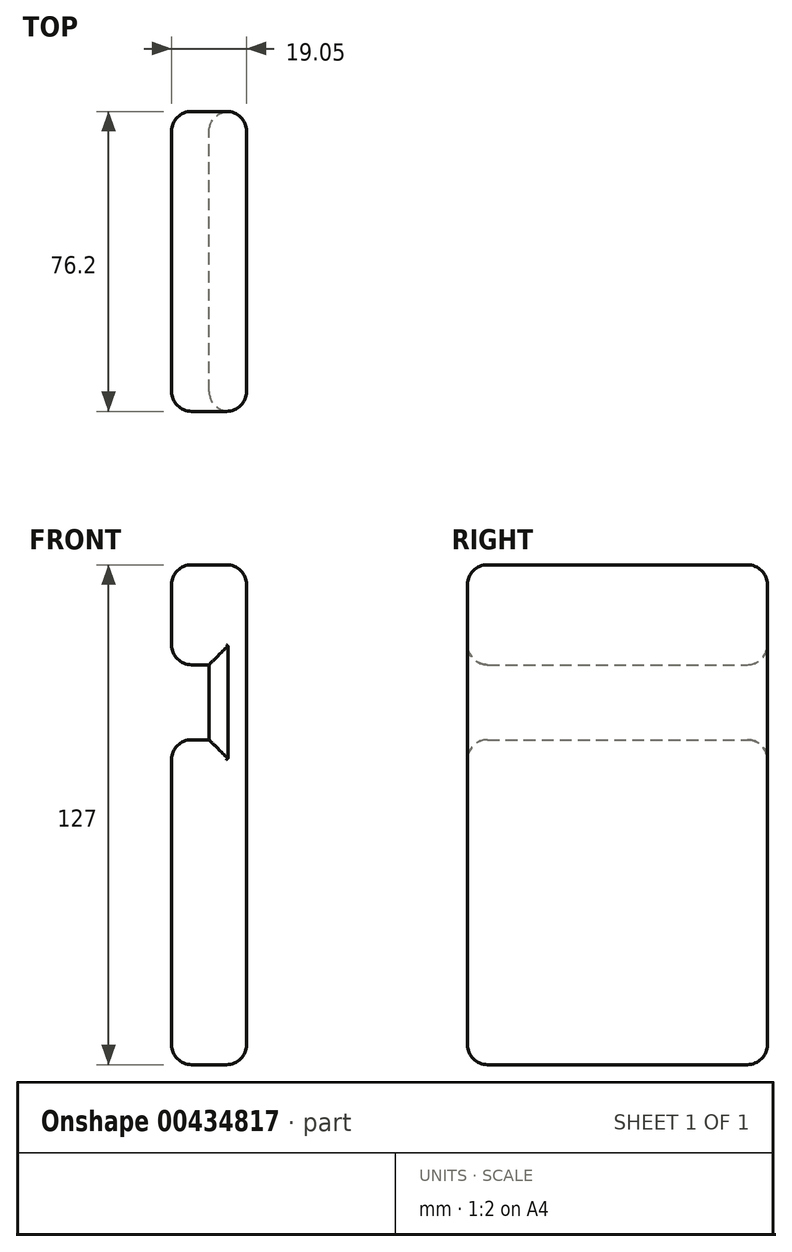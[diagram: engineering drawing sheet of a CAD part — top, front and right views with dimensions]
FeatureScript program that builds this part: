
annotation { "Feature Type Name" : "Feature", "Feature Type Description" : "" }
export const myFeature = defineFeature(function(context is Context, id is Id, definition is map)
    precondition{}
    {
        {
            var Q0;
            Q0=qCreatedBy(makeId("Front.planeOp"),FACE);
            var sketch = newSketch(context, id + "F0", { "sketchPlane" : qUnion([Q0])});
            skLineSegment(sketch, "E0", {"start": v(0, -50.62) * mm, "end": v(0, 76.38) * mm});
            skLineSegment(sketch, "E1", {"start": v(0, 76.38) * mm, "end": v(-19.05, 76.38) * mm});
            skLineSegment(sketch, "E2", {"start": v(-19.05, 76.38) * mm, "end": v(-19.05, 50.98) * mm});
            skLineSegment(sketch, "E3", {"start": v(-19.05, 50.98) * mm, "end": v(-9.52, 50.98) * mm});
            skLineSegment(sketch, "E4", {"start": v(-9.52, 50.98) * mm, "end": v(-9.52, 31.93) * mm});
            skLineSegment(sketch, "E5", {"start": v(-19.05, 31.93) * mm, "end": v(-9.52, 31.93) * mm});
            skLineSegment(sketch, "E6", {"start": v(0, -50.62) * mm, "end": v(-19.05, -50.62) * mm});
            skLineSegment(sketch, "E7", {"start": v(-19.05, 31.93) * mm, "end": v(-19.05, -50.62) * mm});
            skSolve(sketch);
        }
        {
            var Q0;
            Q0=makeQuery(id+"F0.imprint","IMPRINT",FACE,{"disambiguationData":[TD([[makeQuery(id+"F0.imprint","IMPRINT",EDGE,{"derivedFrom":sQuery(id+"F0.wireOp",EDGE,"E0")}),1.0]])]});
            extrude(context, id + "F1", {"entities" : qUnion([Q0]), "depth" : 76.2 * mm});
        }
        {
            var Q0;
            Q0=makeQuery(id+"F1.opExtrude","CAP_FACE",FACE,{"disambiguationData":[OSD([sQuery(id+"F0.wireOp",EDGE,"E0"),sQuery(id+"F0.wireOp",EDGE,"E1"),sQuery(id+"F0.wireOp",EDGE,"E2"),sQuery(id+"F0.wireOp",EDGE,"E3"),sQuery(id+"F0.wireOp",EDGE,"E4"),sQuery(id+"F0.wireOp",EDGE,"E5"),sQuery(id+"F0.wireOp",EDGE,"E6"),sQuery(id+"F0.wireOp",EDGE,"E7")])],"isStart":false});
            var Q1;
            Q1=makeQuery(id+"F1.opExtrude","SWEPT_FACE",FACE,{"disambiguationData":[OSD([sQuery(id+"F0.wireOp",EDGE,"E1")])]});
            var Q2;
            Q2=makeQuery(id+"F1.opExtrude","SWEPT_FACE",FACE,{"disambiguationData":[OSD([sQuery(id+"F0.wireOp",EDGE,"E7")])]});
            var Q3;
            Q3=makeQuery(id+"F1.opExtrude","CAP_FACE",FACE,{"disambiguationData":[OSD([sQuery(id+"F0.wireOp",EDGE,"E0"),sQuery(id+"F0.wireOp",EDGE,"E1"),sQuery(id+"F0.wireOp",EDGE,"E2"),sQuery(id+"F0.wireOp",EDGE,"E3"),sQuery(id+"F0.wireOp",EDGE,"E4"),sQuery(id+"F0.wireOp",EDGE,"E5"),sQuery(id+"F0.wireOp",EDGE,"E6"),sQuery(id+"F0.wireOp",EDGE,"E7")])],"isStart":true});
            var Q4;
            Q4=makeQuery(id+"F1.opExtrude","SWEPT_FACE",FACE,{"disambiguationData":[OSD([sQuery(id+"F0.wireOp",EDGE,"E0")])]});
            fillet(context, id + "F2", {"entities" : qUnion([Q0, Q1, Q2, Q3, Q4]), "radius" : 5.08 * mm, "tangentPropagation" : true, "allowEdgeOverflow" : false});
        }
        {
            var Q0;
            Q0=makeQuery(id+"F1.opExtrude","SWEPT_FACE",FACE,{"disambiguationData":[OSD([sQuery(id+"F0.wireOp",EDGE,"E2")])]});
            fillet(context, id + "F3", {"entities" : qUnion([Q0]), "radius" : 5.08 * mm, "tangentPropagation" : true, "allowEdgeOverflow" : false});
        }
    });
